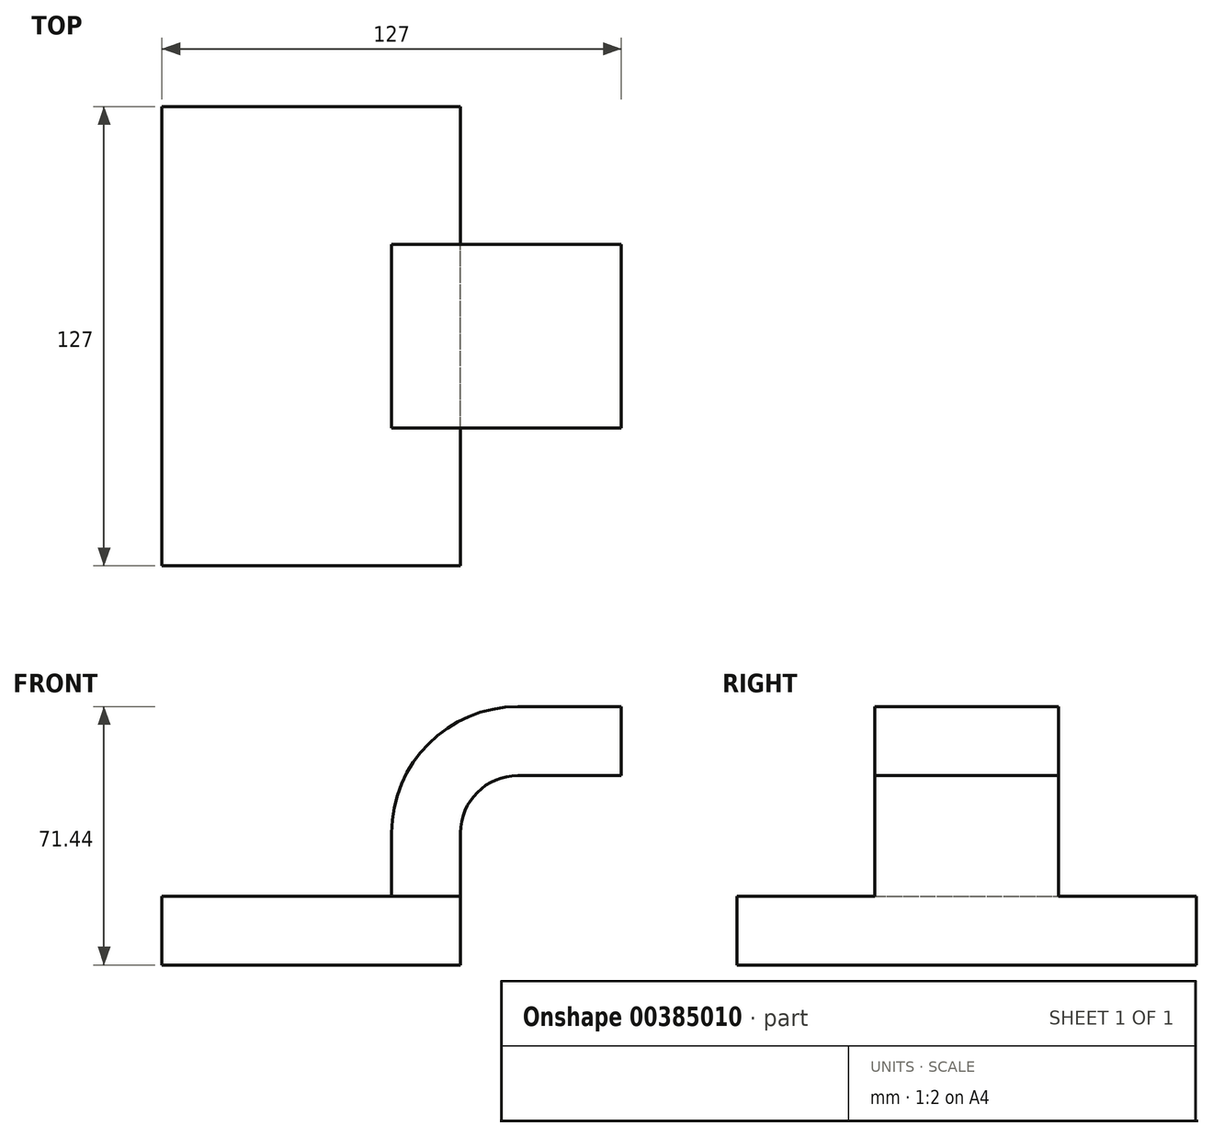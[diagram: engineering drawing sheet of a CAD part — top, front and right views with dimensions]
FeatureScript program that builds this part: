
annotation { "Feature Type Name" : "Feature", "Feature Type Description" : "" }
export const myFeature = defineFeature(function(context is Context, id is Id, definition is map)
    precondition{}
    {
        {
            var Q0;
            Q0=qCreatedBy(makeId("Front.planeOp"),FACE);
            var sketch = newSketch(context, id + "F0", { "sketchPlane" : qUnion([Q0])});
            skLineSegment(sketch, "E0.bottom", {"start": v(41.27, 9.53) * mm, "end": v(-41.28, 9.53) * mm});
            skLineSegment(sketch, "E0.top", {"start": v(41.28, -9.52) * mm, "end": v(-41.27, -9.52) * mm});
            skLineSegment(sketch, "E0.left", {"start": v(41.28, 9.53) * mm, "end": v(41.28, -9.52) * mm});
            skLineSegment(sketch, "E0.right", {"start": v(-41.28, 9.53) * mm, "end": v(-41.27, -9.52) * mm});
            skPoint(sketch, "E0.middle", {"position": v(0, 0) * mm});
            skLineSegment(sketch, "E1.bottom", {"start": v(111.12, 66.68) * mm, "end": v(60.32, 66.68) * mm});
            skLineSegment(sketch, "E1.top", {"start": v(111.12, 38.1) * mm, "end": v(60.32, 38.1) * mm});
            skLineSegment(sketch, "E1.left", {"start": v(111.12, 66.68) * mm, "end": v(111.12, 38.1) * mm});
            skLineSegment(sketch, "E1.right", {"start": v(60.32, 66.68) * mm, "end": v(60.32, 38.1) * mm});
            skPoint(sketch, "E1.middle", {"position": v(85.72, 52.39) * mm});
            skLineSegment(sketch, "E2", {"start": v(41.27, 9.53) * mm, "end": v(41.27, 26.99) * mm});
            skArc(sketch, "E3", {"start": v(57.15, 42.86) * mm, "mid": v(45.92, 38.21) * mm, "end": v(41.27, 26.99) * mm});
            skLineSegment(sketch, "E4", {"start": v(57.15, 42.86) * mm, "end": v(85.73, 42.86) * mm});
            skLineSegment(sketch, "E5.0", {"start": v(22.23, 9.53) * mm, "end": v(22.23, 26.99) * mm});
            skArc(sketch, "E5.1", {"start": v(57.15, 61.91) * mm, "mid": v(32.45, 51.68) * mm, "end": v(22.23, 26.99) * mm});
            skLineSegment(sketch, "E5.2", {"start": v(57.15, 61.91) * mm, "end": v(85.73, 61.91) * mm});
            skFitSpline(sketch, "E6", {"points": [v(-41.28, 9.52) * mm, v(57.15, 61.91) * mm], "startDerivative": vector(45.43, 112.11) * mm, "endDerivative": vector(156.47, -19.96) * mm});
            skLineSegment(sketch, "E7", {"start": v(85.73, 61.91) * mm, "end": v(85.73, 42.86) * mm});
            skSolve(sketch);
        }
        {
            var Q0;
            Q0=makeQuery(id+"F0.imprint","IMPRINT",FACE,{"disambiguationData":[TD([[makeQuery(id+"F0.imprint","IMPRINT",EDGE,{"derivedFrom":sQuery(id+"F0.wireOp",EDGE,"E0.top")}),-1.0]])]});
            extrude(context, id + "F1", {"entities" : qUnion([Q0]), "endBound" : BoundingType.SYMMETRIC, "depth" : 127 * mm});
        }
        {
            var Q0;
            {var subQ1=sQuery(id+"F0.wireOp",EDGE,"E2");Q0=makeQuery(id+"F0.imprint","IMPRINT",FACE,{"disambiguationData":[TD([[makeQuery(id+"F0.imprint","IMPRINT",EDGE,{"derivedFrom":subQ1}),1.0]])]});}
            var Q1;
            {var subQ5=sQuery(id+"F0.wireOp",EDGE,"E7");Q1=makeQuery(id+"F0.imprint","IMPRINT",FACE,{"disambiguationData":[TD([[makeQuery(id+"F0.imprint","IMPRINT",EDGE,{"derivedFrom":subQ5}),-1.0]])]});}
            extrude(context, id + "F2", {"entities" : qUnion([Q0, Q1]), "operationType" : NewBodyOperationType.ADD, "endBound" : BoundingType.SYMMETRIC, "depth" : 50.8 * mm});
        }
    });
